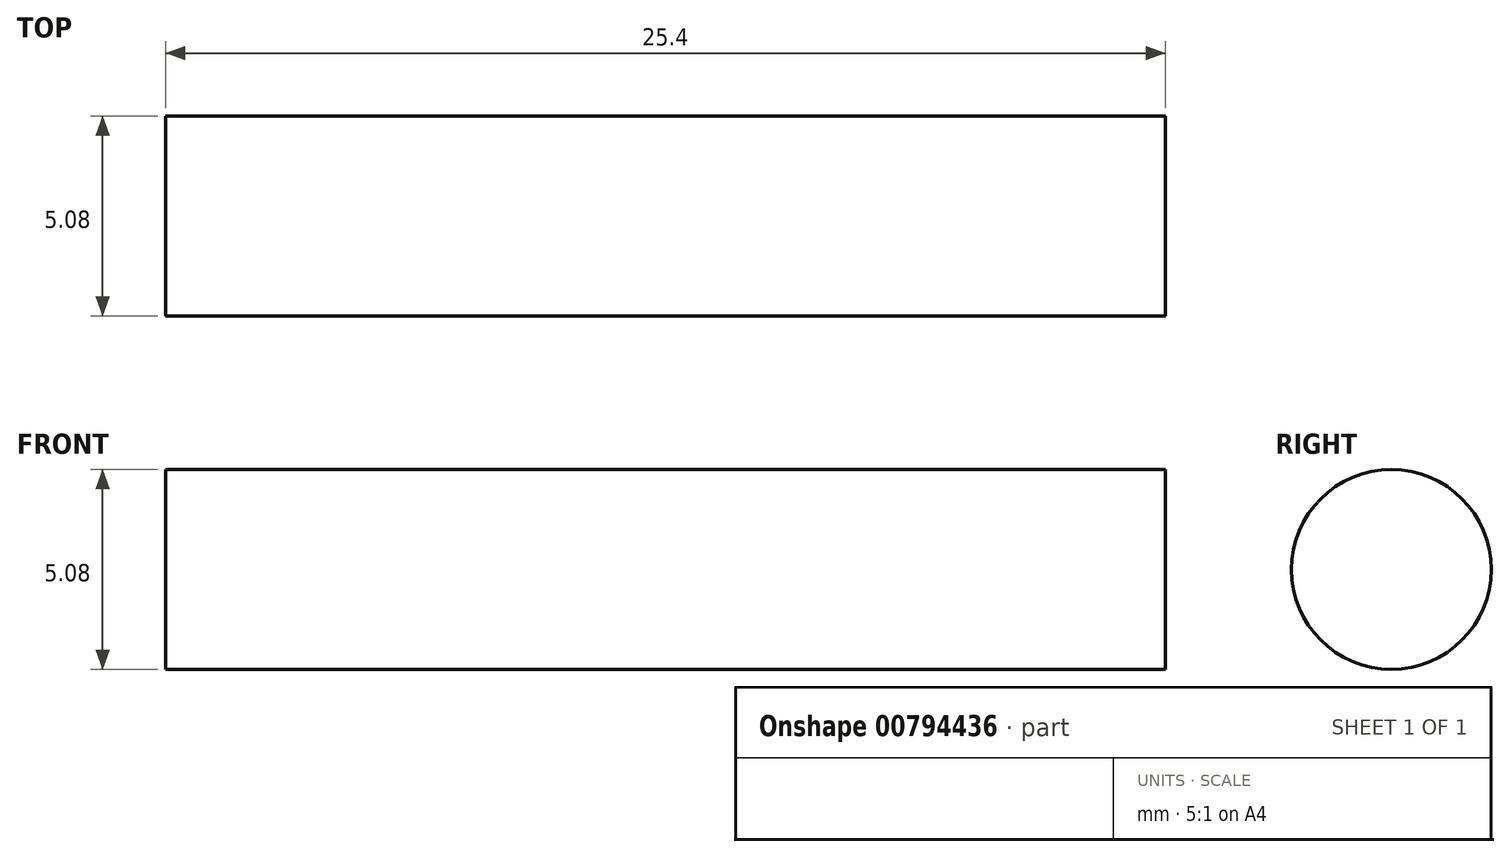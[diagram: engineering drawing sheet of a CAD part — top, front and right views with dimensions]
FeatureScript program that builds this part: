
annotation { "Feature Type Name" : "Feature", "Feature Type Description" : "" }
export const myFeature = defineFeature(function(context is Context, id is Id, definition is map)
    precondition{}
    {
        {
            var Q0;
            Q0=qCreatedBy(makeId("Right.planeOp"),FACE);
            var sketch = newSketch(context, id + "F0", { "sketchPlane" : qUnion([Q0])});
            skCircle(sketch, "E0", {"center": v(0, 0) * mm, "radius": 2.54 * mm});
            skSolve(sketch);
        }
        {
            var Q0;
            Q0=makeQuery(id+"F0.imprint","IMPRINT",FACE,{"disambiguationData":[TD([[makeQuery(id+"F0.imprint","IMPRINT",EDGE,{"derivedFrom":sQuery(id+"F0.wireOp",EDGE,"E0")}),1.0]])]});
            extrude(context, id + "F1", {"entities" : qUnion([Q0]), "depth" : 25.4 * mm, "offsetDistance" : 25.4 * mm});
        }
    });
